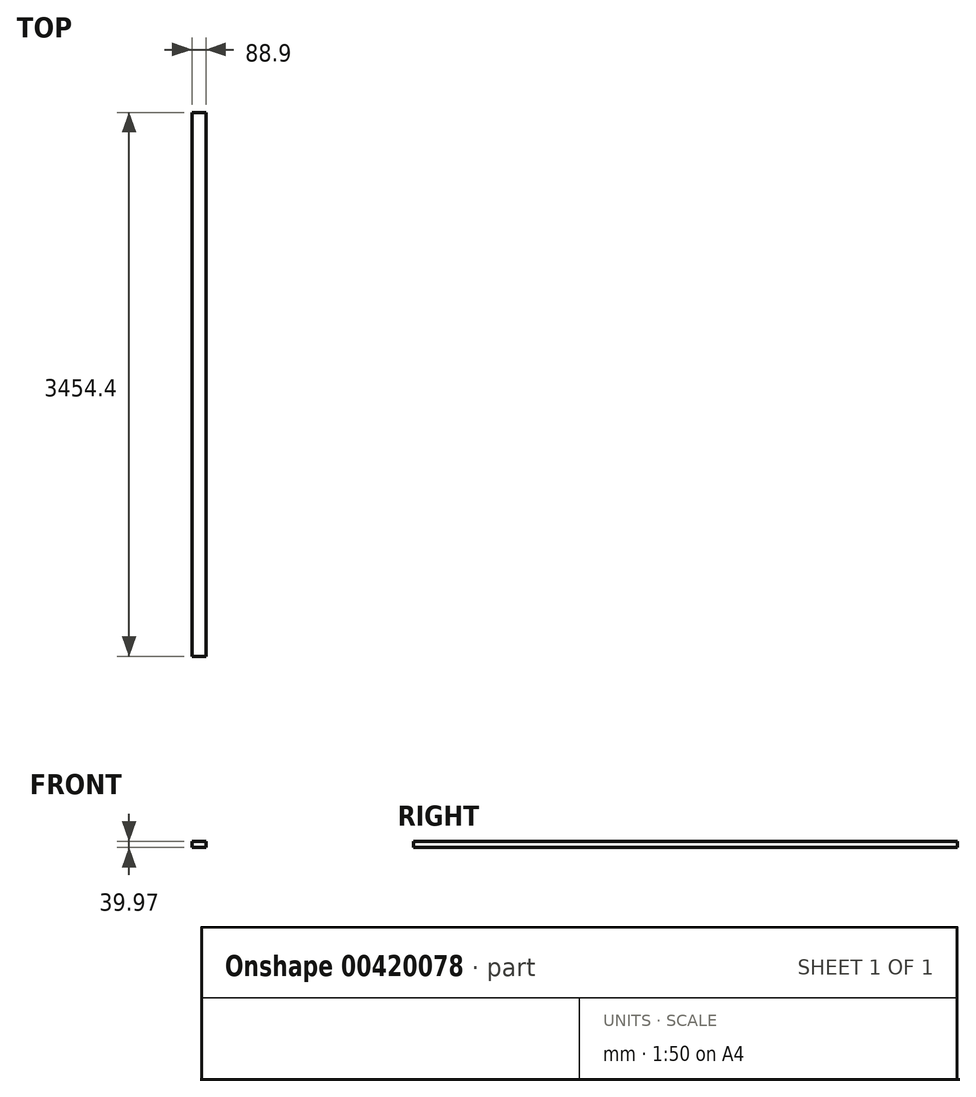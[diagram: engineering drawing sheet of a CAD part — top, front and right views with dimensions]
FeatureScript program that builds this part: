
annotation { "Feature Type Name" : "Feature", "Feature Type Description" : "" }
export const myFeature = defineFeature(function(context is Context, id is Id, definition is map)
    precondition{}
    {
        {
            var Q0;
            Q0=qCreatedBy(makeId("Front.planeOp"),FACE);
            var sketch = newSketch(context, id + "F0", { "sketchPlane" : qUnion([Q0])});
            skLineSegment(sketch, "E0.bottom", {"start": v(0, 0) * mm, "end": v(88.9, 0) * mm});
            skLineSegment(sketch, "E0.top", {"start": v(0, 39.97) * mm, "end": v(88.9, 39.97) * mm});
            skLineSegment(sketch, "E0.left", {"start": v(0, 0) * mm, "end": v(0, 39.97) * mm});
            skLineSegment(sketch, "E0.right", {"start": v(88.9, 0) * mm, "end": v(88.9, 39.97) * mm});
            skSolve(sketch);
        }
        {
            var Q0;
            Q0=makeQuery(id+"F0.imprint","IMPRINT",FACE,{"disambiguationData":[TD([[makeQuery(id+"F0.imprint","IMPRINT",EDGE,{"derivedFrom":sQuery(id+"F0.wireOp",EDGE,"E0.bottom")}),1.0]])]});
            extrude(context, id + "F1", {"entities" : qUnion([Q0]), "depth" : 3454.4 * mm});
        }
    });
